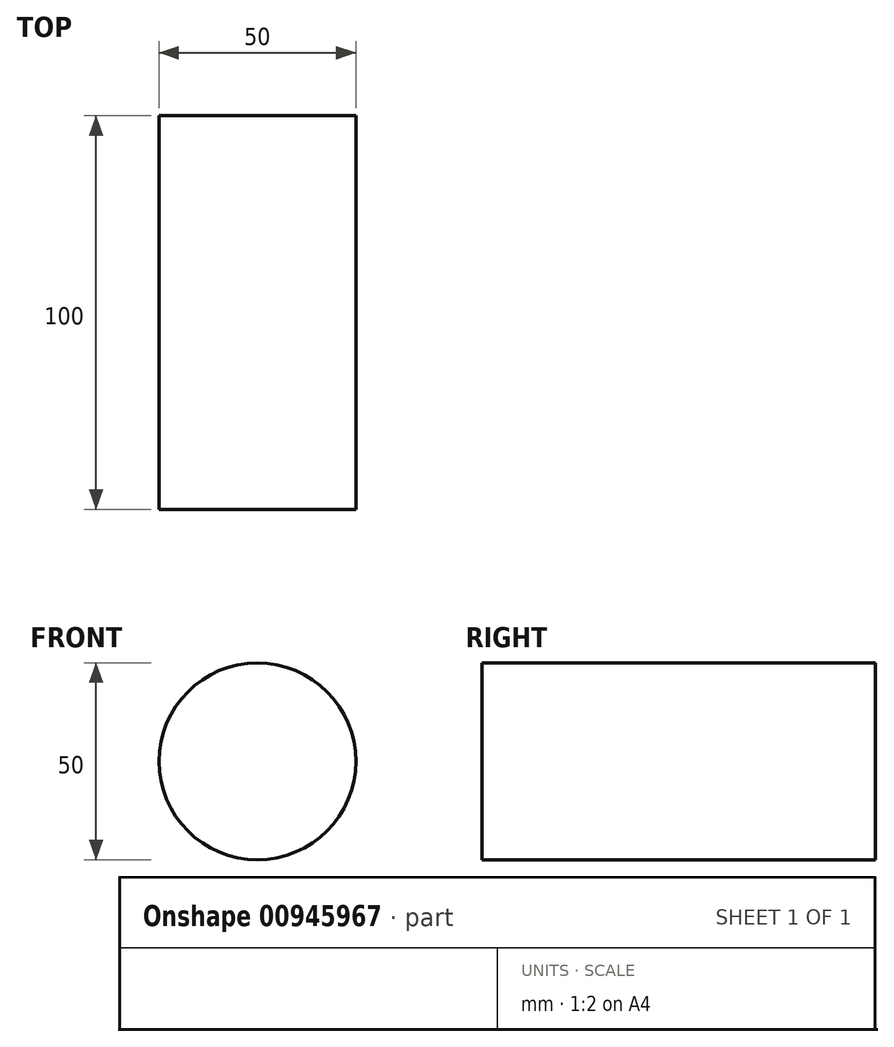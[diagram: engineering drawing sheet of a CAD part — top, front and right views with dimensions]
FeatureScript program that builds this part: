
annotation { "Feature Type Name" : "Feature", "Feature Type Description" : "" }
export const myFeature = defineFeature(function(context is Context, id is Id, definition is map)
    precondition{}
    {
        {
            var Q0;
            Q0=qCreatedBy(makeId("Front.planeOp"),FACE);
            var sketch = newSketch(context, id + "F0", { "sketchPlane" : qUnion([Q0])});
            skCircle(sketch, "E0", {"center": v(0, 0) * mm, "radius": 25 * mm});
            skSolve(sketch);
        }
        {
            var Q0;
            Q0=makeQuery(id+"F0.imprint","IMPRINT",FACE,{"disambiguationData":[TD([[makeQuery(id+"F0.imprint","IMPRINT",EDGE,{"derivedFrom":sQuery(id+"F0.wireOp",EDGE,"E0")}),1.0]])]});
            extrude(context, id + "F1", {"entities" : qUnion([Q0]), "endBound" : BoundingType.SYMMETRIC, "depth" : 100 * mm, "offsetDistance" : 25 * mm});
        }
    });
